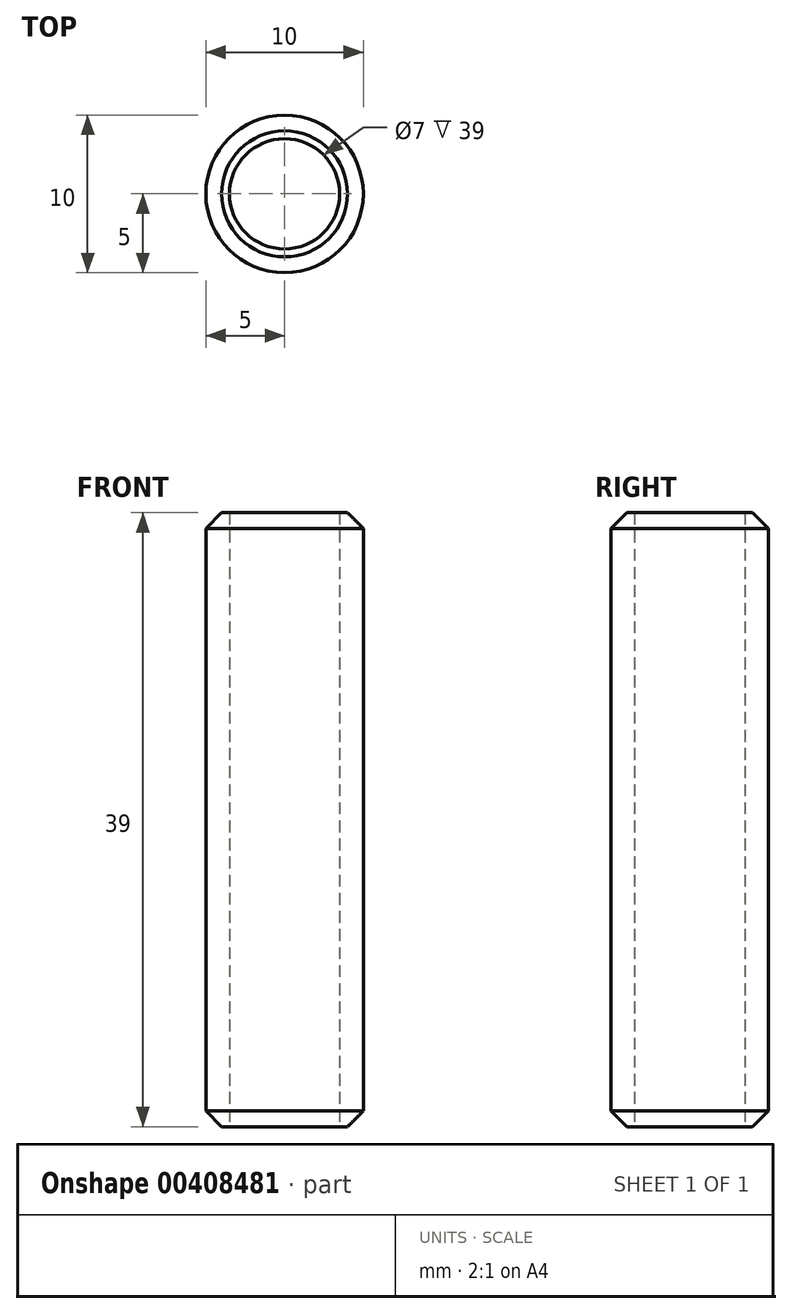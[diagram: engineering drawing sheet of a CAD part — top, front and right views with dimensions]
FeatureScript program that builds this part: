
annotation { "Feature Type Name" : "Feature", "Feature Type Description" : "" }
export const myFeature = defineFeature(function(context is Context, id is Id, definition is map)
    precondition{}
    {
        {
            var Q0;
            Q0=qCreatedBy(makeId("Top.planeOp"),FACE);
            var sketch = newSketch(context, id + "F0", { "sketchPlane" : qUnion([Q0])});
            skCircle(sketch, "E0", {"center": v(0, 0) * mm, "radius": 5 * mm});
            skCircle(sketch, "E1", {"center": v(0, 0) * mm, "radius": 3.5 * mm});
            skSolve(sketch);
        }
        {
            var Q0;
            Q0=makeQuery(id+"F0.imprint","IMPRINT",FACE,{"disambiguationData":[TD([[makeQuery(id+"F0.imprint","IMPRINT",EDGE,{"derivedFrom":sQuery(id+"F0.wireOp",EDGE,"E0")}),1.0]])]});
            extrude(context, id + "F1", {"entities" : qUnion([Q0]), "endBound" : BoundingType.SYMMETRIC, "depth" : 39 * mm});
        }
        {
            var Q0;
            Q0=makeQuery(id+"F1.opExtrude","CAP_EDGE",EDGE,{"disambiguationData":[OSD([sQuery(id+"F0.wireOp",EDGE,"E0")])],"isStart":false});
            var Q1;
            Q1=makeQuery(id+"F1.opExtrude","CAP_EDGE",EDGE,{"disambiguationData":[OSD([sQuery(id+"F0.wireOp",EDGE,"E0")])],"isStart":true});
            chamfer(context, id + "F2", {"entities" : qUnion([Q0, Q1]), "chamferType" : ChamferType.OFFSET_ANGLE, "width" : 1 * mm, "oppositeDirection" : false, "angle" : 45 * degree, "tangentPropagation" : true});
        }
    });
